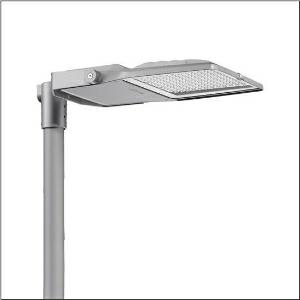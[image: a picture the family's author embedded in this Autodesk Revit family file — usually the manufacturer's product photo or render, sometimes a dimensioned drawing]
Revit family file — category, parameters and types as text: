
# Revit family: floodlight_fl_21_midi___pl43_5xa7786f2a3a_0f3f
name_source: partatom
category: Lighting Fixtures
units: mm (PartAtom-declared; Revit-internal decimal feet)

## family parameters
Cut with Voids When Loaded = No
Host = Face
Light Source = No
Part Type = Normal
Room Calculation Point = No
Round Connector Dimension = Use Diameter
Shared = No

## types (1)
- --- (1 x LED, 36680 lm, 271.6 W, 3000K)
    Apparent Load = 272 VA
    CIE Flux Codes = 27 78 99 100 100
    Color Rendering = 70
    Color Temperature = 3000K
    Default Elevation = 1800 mm
    Description = Floodlight FL 21 midi, floodlight, primary light control with lens, of PMMA, primary optical cover: protective disc, of toughened safety glass, transparent, light distribution: PL43, light emission: direct distribution, installation type: surface-mounted, LED, High Power LED, rated luminous flux: 36.680lm, luminous efficacy: 135lm/W, light colour: 730, colour temperature: 3000K, control gear: Smart Interface (Zhaga), control: flexible luminous flux parameterisation, time-dependent luminous flux control, constant luminous flux control, overheat protection, pre-setting: logarithmic dimming characteristic, with terminal, 6-pole, mains connection: 220..240V, AC, 50/60Hz, start of lifetime: 272W, end of service life: 287W, reduction: 123W, luminaire housing, of diecast aluminium, powder-coated, SITECO metallic grey (DB 702S), corrosivity category C5 mid according to DIN EN ISO 12944, suitable for swimming pools, chlorine-resistant, sealing non-destructively replaceable, please order mast flange separately, mast bracket, of steel, galvanised, powder-coated, SITECO metallic grey (DB 702S), Smart Interface below and above, protection rating (complete): IP66, insulation class (complete): insulation class II (safety insulation), certification: CE, ENEC, VDE, protection symbol: D, impact resistance: IK08, permissible operating ambient temperature: -40..+40°C, permissible operating ambient temperature for outdoor applications: -40..+50°C, standard: DIN EN 12944, LABS conformity tested according to VDMA 24364:2018-05, packaging unit: 1 piece

Light Distribution: PL43
    Height = 76 mm
    Lamp = 1 x LED
    Lamp Light Flux = 36680 lm
    Lamp Power = 271.6 W
    Lamp count = 1
    Length = 657 mm
    Luminous efficacy = 135 lm/W
    Manufacturer = Siteco
    ModVariant = No
    Model = 5XA7786F2A3A
    Number of Poles = 1
    OnlyDefault = Yes
    Power Factor = 1
    Product Name = Floodlight FL 21 midi | PL43
    Product group = floodlight | pylon annexe
    ProductGroupID = 6201
    Protection Class = Protection class II
    Protection Degree = IP 66
    RLX_Detail_Level = 1
    RLX_Emergency_Light_Flux = 0 lm
    RLX_Emergency_Type = 0
    RLX_Emergency_Type_DB = No
    RlxData = <blob elided: 153689 chars, md5=be5ef9b8>
    Socket = socket
    Standby Power = 0 W
    System Light Flux = 36680 lm
    System Power = 272 W
    Type Comments = factory setting: luminous flux: 100 % | dim-lin: 254 | 620 mA
    Type Image = l_1007123.jpg
    URL = http://relux.com
    VarID = @adj_176579
    Voltage = 0 V
    Weight = 0.00 kg
    Width = 442 mm

## geometry (parser evidence)
native form markers: Blend x4, Sweep x15
no freeform markers — native parametric forms only
